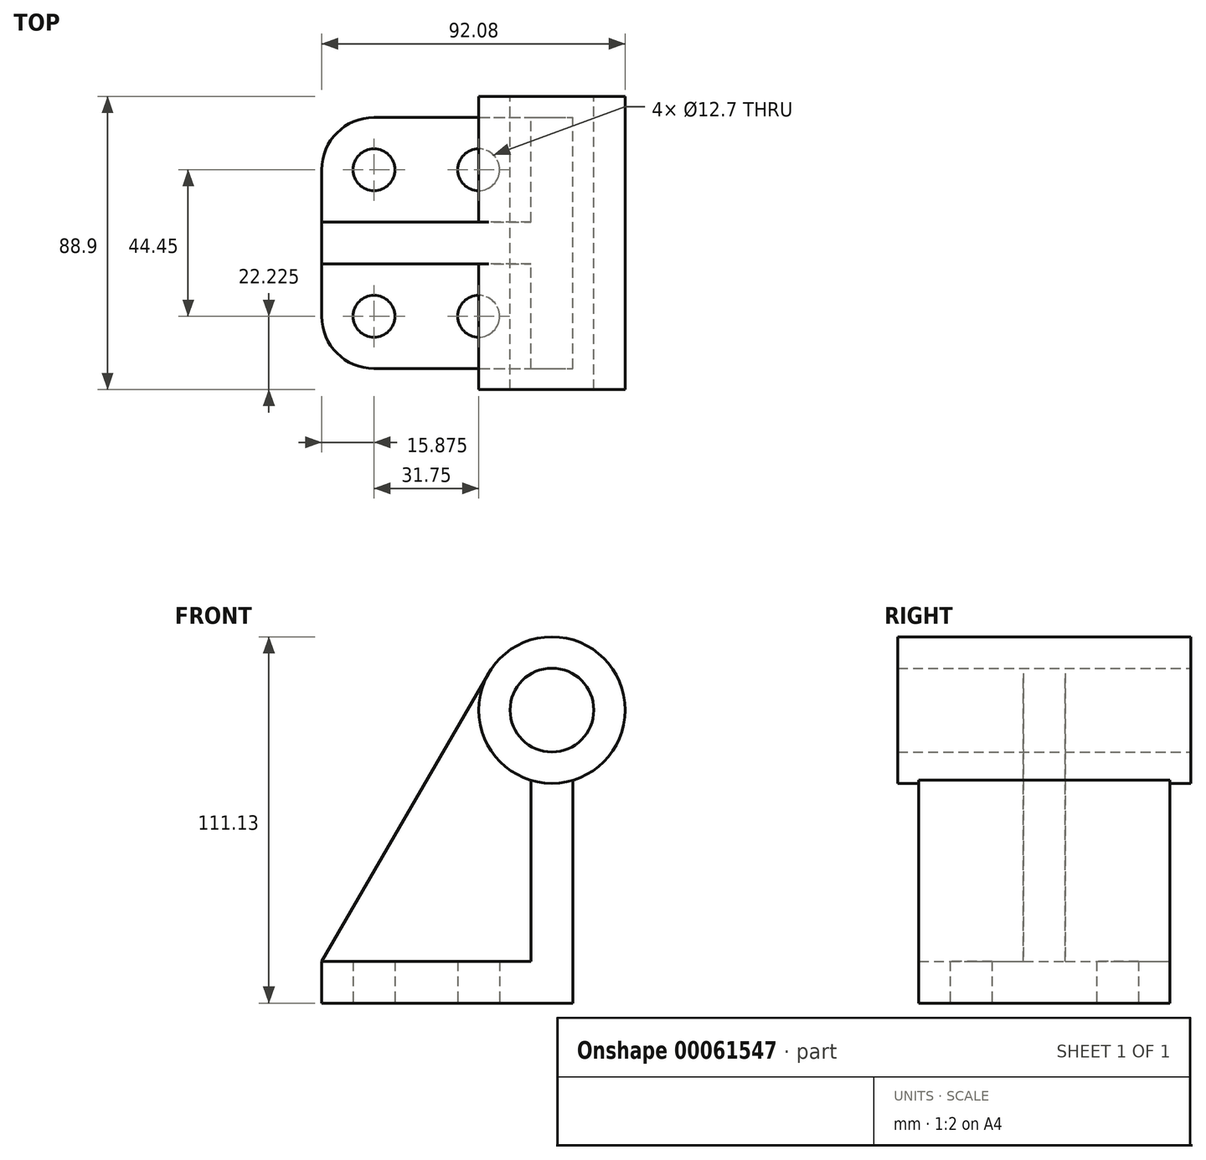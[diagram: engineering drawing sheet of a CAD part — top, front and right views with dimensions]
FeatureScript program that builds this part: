
annotation { "Feature Type Name" : "Feature", "Feature Type Description" : "" }
export const myFeature = defineFeature(function(context is Context, id is Id, definition is map)
    precondition{}
    {
        {
            var Q0;
            Q0=qCreatedBy(makeId("Front.planeOp"),FACE);
            var sketch = newSketch(context, id + "F0", { "sketchPlane" : qUnion([Q0])});
            skCircle(sketch, "E0", {"center": v(0, 0) * mm, "radius": 12.7 * mm});
            skCircle(sketch, "E1", {"center": v(0, 0) * mm, "radius": 22.23 * mm});
            skSolve(sketch);
        }
        {
            var Q0;
            Q0 = qSketchRegion(id + "F0", true);
            extrude(context, id + "F1", {"entities" : qUnion([Q0]), "endBound" : BoundingType.SYMMETRIC, "depth" : 88.9 * mm});
        }
        {
            var Q0;
            Q0=qCreatedBy(makeId("Front.planeOp"),FACE);
            var sketch = newSketch(context, id + "F2", { "sketchPlane" : qUnion([Q0])});
            skArc(sketch, "E2.0", {"start": v(-6.35, -21.3) * mm, "mid": v(0, -22.23) * mm, "end": v(6.35, -21.3) * mm});
            skLineSegment(sketch, "E3", {"start": v(-6.35, -21.3) * mm, "end": v(-6.35, -88.9) * mm});
            skLineSegment(sketch, "E4", {"start": v(-6.35, -88.9) * mm, "end": v(6.35, -88.9) * mm});
            skLineSegment(sketch, "E5", {"start": v(6.35, -88.9) * mm, "end": v(6.35, -21.3) * mm});
            skLineSegment(sketch, "E6", {"start": v(0, -88.9) * mm, "end": v(0, 0) * mm});
            skSolve(sketch);
        }
        {
            var Q0;
            Q0 = qSketchRegion(id + "F2", true);
            extrude(context, id + "F3", {"entities" : qUnion([Q0]), "operationType" : NewBodyOperationType.ADD, "endBound" : BoundingType.SYMMETRIC, "depth" : 76.2 * mm});
        }
        {
            var Q0;
            Q0=makeQuery(id+"F3.opExtrude","SWEPT_FACE",FACE,{"disambiguationData":[OSD([sQuery(id+"F2.wireOp",EDGE,"E4")])]});
            var sketch = newSketch(context, id + "F4", { "sketchPlane" : qUnion([Q0])});
            skLineSegment(sketch, "E7", {"start": v(6.35, 38.1) * mm, "end": v(-53.97, 38.1) * mm});
            skLineSegment(sketch, "E8", {"start": v(-69.85, 22.23) * mm, "end": v(-69.85, -22.23) * mm});
            skLineSegment(sketch, "E9", {"start": v(-53.97, -38.1) * mm, "end": v(6.35, -38.1) * mm});
            skLineSegment(sketch, "E10", {"start": v(6.35, -38.1) * mm, "end": v(6.35, 38.1) * mm});
            skCircle(sketch, "E11", {"center": v(-53.97, 22.23) * mm, "radius": 6.35 * mm});
            skCircle(sketch, "E12", {"center": v(-53.97, -22.23) * mm, "radius": 6.35 * mm});
            skCircle(sketch, "E13", {"center": v(-22.22, -22.22) * mm, "radius": 6.35 * mm});
            skCircle(sketch, "E14", {"center": v(-22.22, 22.23) * mm, "radius": 6.35 * mm});
            skPoint(sketch, "E15.visualSharp", {"position": v(-69.85, 38.1) * mm});
            skArc(sketch, "E15.filletArc", {"start": v(-53.97, 38.1) * mm, "mid": v(-65.2, 33.45) * mm, "end": v(-69.85, 22.22) * mm});
            skPoint(sketch, "E16.visualSharp", {"position": v(-69.85, -38.1) * mm});
            skArc(sketch, "E16.filletArc", {"start": v(-69.85, -22.23) * mm, "mid": v(-65.2, -33.45) * mm, "end": v(-53.97, -38.1) * mm});
            skSolve(sketch);
        }
        {
            var Q0;
            Q0 = qSketchRegion(id + "F4", true);
            extrude(context, id + "F5", {"entities" : qUnion([Q0]), "operationType" : NewBodyOperationType.ADD, "oppositeDirection" : true, "depth" : 12.7 * mm});
        }
        {
            var Q0;
            Q0=qCreatedBy(makeId("Front.planeOp"),FACE);
            var sketch = newSketch(context, id + "F6", { "sketchPlane" : qUnion([Q0])});
            skArc(sketch, "E17.0", {"start": v(-19.23, 11.14) * mm, "mid": v(-20.66, -8.2) * mm, "end": v(-6.35, -21.3) * mm});
            skLineSegment(sketch, "E18.0", {"start": v(-6.35, -21.3) * mm, "end": v(-6.35, -76.2) * mm});
            skLineSegment(sketch, "E19.0", {"start": v(-53.97, -76.2) * mm, "end": v(-6.35, -76.2) * mm});
            skLineSegment(sketch, "E20.0", {"start": v(-53.97, -76.2) * mm, "end": v(-69.85, -76.2) * mm});
            skLineSegment(sketch, "E21", {"start": v(-69.85, -76.2) * mm, "end": v(-19.23, 11.14) * mm});
            skSolve(sketch);
        }
        {
            var Q0;
            Q0 = qSketchRegion(id + "F6", true);
            extrude(context, id + "F7", {"entities" : qUnion([Q0]), "operationType" : NewBodyOperationType.ADD, "endBound" : BoundingType.SYMMETRIC, "depth" : 12.7 * mm});
        }
    });
